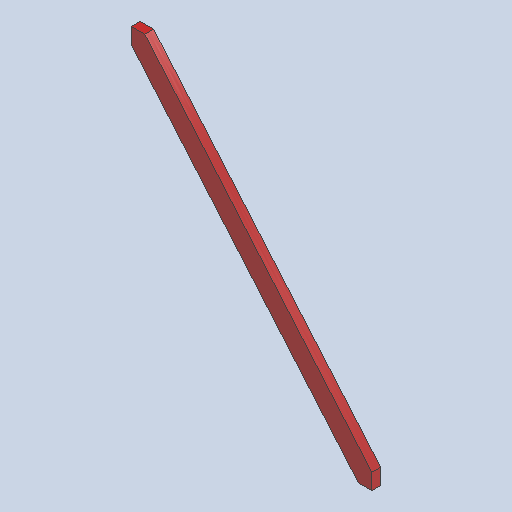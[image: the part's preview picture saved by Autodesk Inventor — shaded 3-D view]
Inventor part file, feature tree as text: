
AUTODESK INVENTOR PART (.ipt)
format: ipt  version: 2025 (Build 290162000, 162)  size: 95,744 bytes
history: native  units: in
note: dims shown in document units (in); Inventor stores cm internally (conversion verified against a paired STEP export)
features: other x4, sketch x1
ambient origin geometry x8: Origin, YZ Plane, XZ Plane, XY Plane, X Axis, Y Axis, Z Axis, Center Point
bodies: Solid1 (feature_tree)
feature tree (5):
  other  "44x2x4.ipt"
  other  "Solid1::44x2x4.ipt"
  other  "TaggingFeature1"
  sketch  "Sketch1"  dims[d0=0.3937in]
  other  "Finish1"
